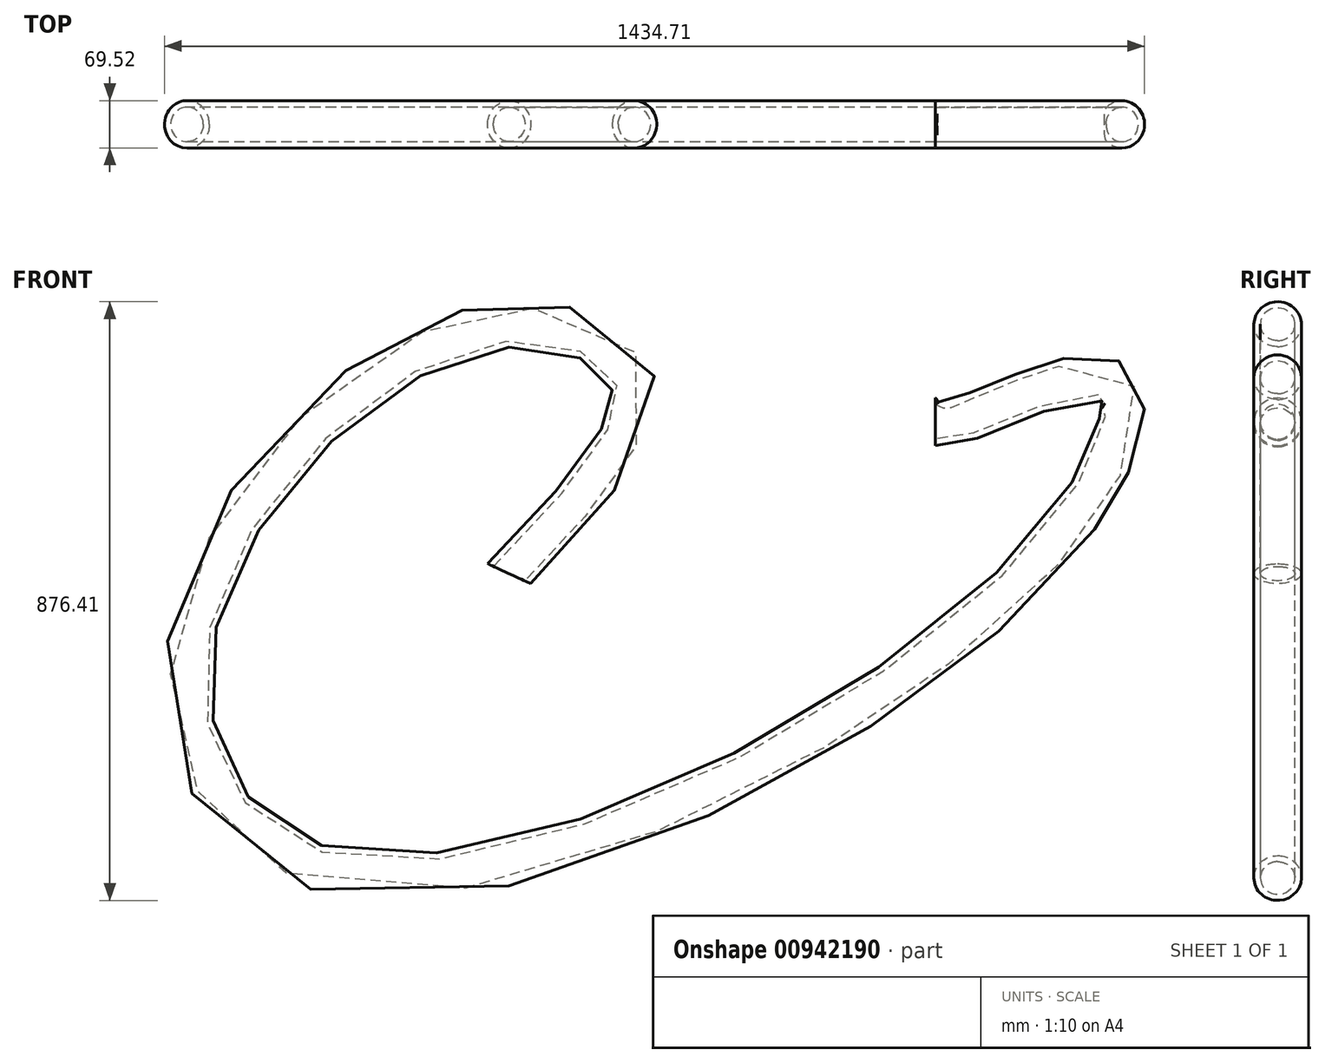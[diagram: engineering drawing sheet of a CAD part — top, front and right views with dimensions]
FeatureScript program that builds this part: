
annotation { "Feature Type Name" : "Feature", "Feature Type Description" : "" }
export const myFeature = defineFeature(function(context is Context, id is Id, definition is map)
    precondition{}
    {
        {
            var Q0;
            Q0=qCreatedBy(makeId("Right.planeOp"),FACE);
            var sketch = newSketch(context, id + "F0", { "sketchPlane" : qUnion([Q0])});
            skCircle(sketch, "E0", {"center": v(0, 0) * mm, "radius": 34.76 * mm});
            skSolve(sketch);
        }
        {
            var Q0;
            Q0=qCreatedBy(makeId("Front.planeOp"),FACE);
            var sketch = newSketch(context, id + "F1", { "sketchPlane" : qUnion([Q0])});
            skFitSpline(sketch, "E1", {"points": [v(0, 0) * mm, v(29.82, 0) * mm, v(246.48, 62.08) * mm, v(170.77, -183.19) * mm, v(-874.05, -660.36) * mm, v(-1087.37, -305.17) * mm, v(-665.09, 135.95) * mm, v(-443.06, 56.57) * mm, v(-623.73, -222.27) * mm], "startDerivative": vector(541.54, -190.18) * mm, "endDerivative": vector(-2433.12, -2519.24) * mm});
            skSolve(sketch);
        }
        {
            var Q0;
            Q0=makeQuery(id+"F0.imprint","IMPRINT",FACE,{"disambiguationData":[TD([[makeQuery(id+"F0.imprint","IMPRINT",EDGE,{"derivedFrom":sQuery(id+"F0.wireOp",EDGE,"E0")}),1.0]])]});
            var Q1;
            Q1=sQuery(id+"F1.wireOp",EDGE,"E1");
            sweep(context, id + "F2", {"profiles" : qUnion([Q0]), "path" : qUnion([Q1])});
        }
        {
            var Q0;
            Q0=makeQuery(id+"F2.opSweep","CAP_FACE",FACE,{"disambiguationData":[OSD([sQuery(id+"F0.wireOp",EDGE,"E0"),sQuery(id+"F1.wireOp",VERTEX,"E1.end")])],"isStart":false});
            var sketch = newSketch(context, id + "F3", { "sketchPlane" : qUnion([Q0])});
            skCircle(sketch, "E2", {"center": v(-474.16, 0) * mm, "radius": 25.31 * mm});
            skSolve(sketch);
        }
        {
            var Q0;
            Q0=makeQuery(id+"F3.imprint","IMPRINT",FACE,{"disambiguationData":[TD([[makeQuery(id+"F3.imprint","IMPRINT",EDGE,{"derivedFrom":sQuery(id+"F3.wireOp",EDGE,"E2")}),1.0]])]});
            var Q1;
            Q1 = qSketchRegion(id + "F1", true);
            var Q2;
            Q2=sQuery(id+"F1.wireOp",EDGE,"E1");
            sweep(context, id + "F4", {"operationType" : NewBodyOperationType.REMOVE, "profiles" : qUnion([Q0, Q1]), "path" : qUnion([Q2])});
        }
    });
